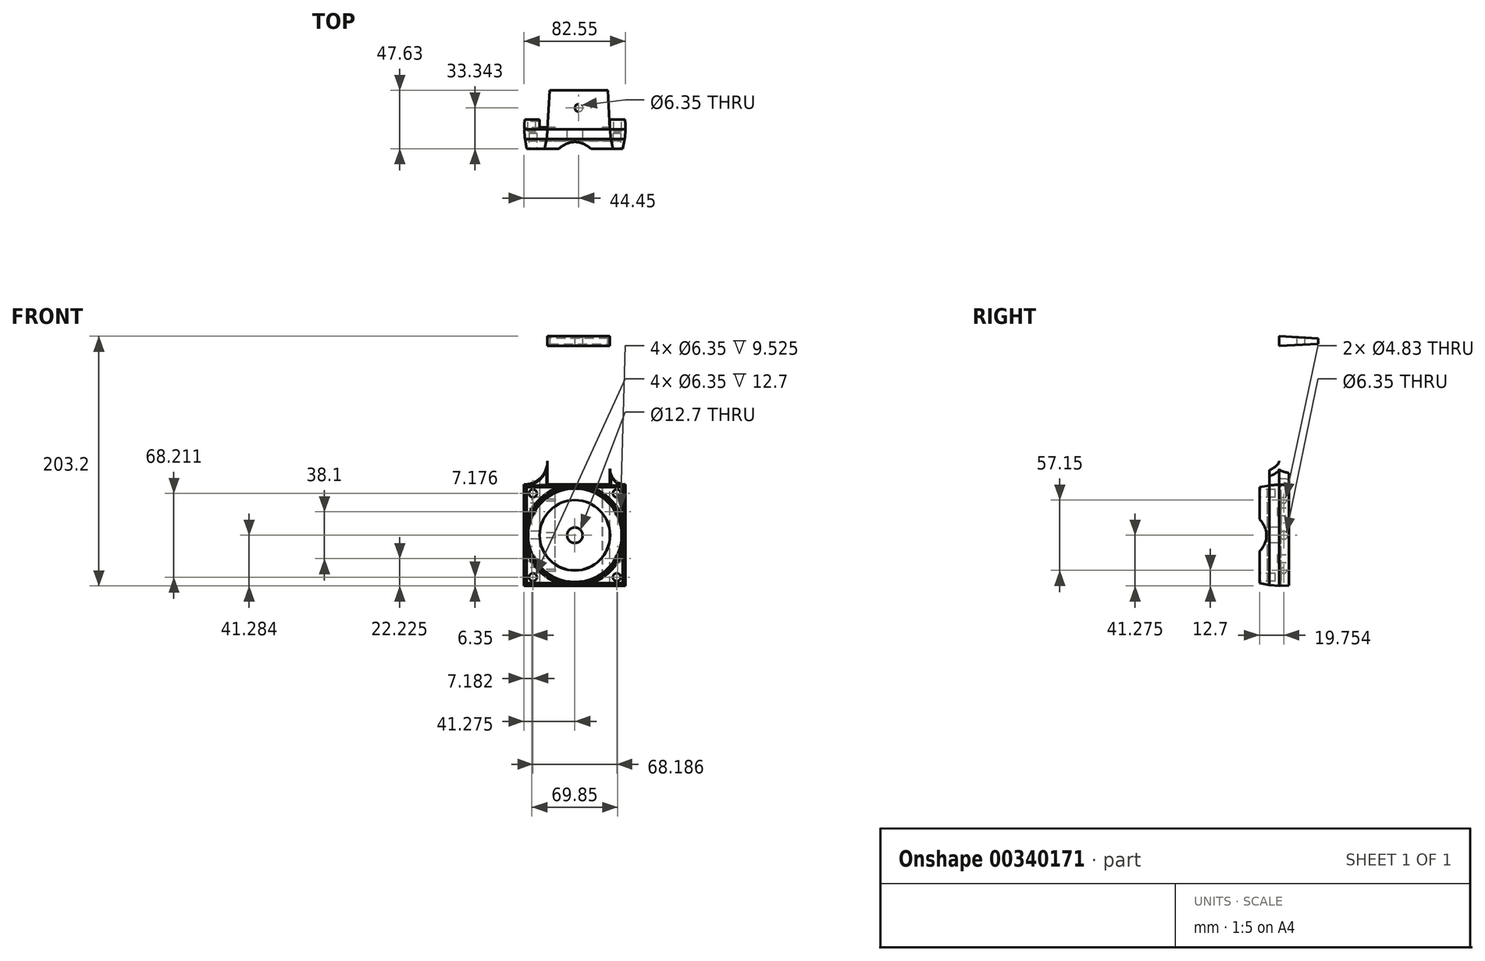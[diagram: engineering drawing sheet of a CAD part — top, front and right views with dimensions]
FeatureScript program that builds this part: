
annotation { "Feature Type Name" : "Feature", "Feature Type Description" : "" }
export const myFeature = defineFeature(function(context is Context, id is Id, definition is map)
    precondition{}
    {
        {
            var Q0;
            Q0=qCreatedBy(makeId("Front.planeOp"),FACE);
            var sketch = newSketch(context, id + "F0", { "sketchPlane" : qUnion([Q0])});
            skLineSegment(sketch, "E0.bottom", {"start": v(0, 0) * mm, "end": v(82.55, 0) * mm});
            skLineSegment(sketch, "E0.top", {"start": v(0, 82.55) * mm, "end": v(82.55, 82.55) * mm});
            skLineSegment(sketch, "E0.left", {"start": v(0, 0) * mm, "end": v(0, 82.55) * mm});
            skLineSegment(sketch, "E0.right", {"start": v(82.55, 0) * mm, "end": v(82.55, 82.55) * mm});
            skLineSegment(sketch, "E1.bottom", {"start": v(19.05, 82.55) * mm, "end": v(69.85, 82.55) * mm});
            skLineSegment(sketch, "E1.top", {"start": v(19.05, 203.2) * mm, "end": v(69.85, 203.2) * mm});
            skLineSegment(sketch, "E1.left", {"start": v(19.05, 82.55) * mm, "end": v(19.05, 203.2) * mm});
            skLineSegment(sketch, "E1.right", {"start": v(69.85, 82.55) * mm, "end": v(69.85, 203.2) * mm});
            skCircle(sketch, "E2", {"center": v(82.55, 95.25) * mm, "radius": 12.7 * mm});
            skCircle(sketch, "E3", {"center": v(0, 101.6) * mm, "radius": 19.05 * mm});
            skSolve(sketch);
        }
        {
            var Q0;
            {var subQ3=sQuery(id+"F0.wireOp",EDGE,"E1.bottom");Q0=makeQuery(id+"F0.imprint","IMPRINT",FACE,{"disambiguationData":[TD([[makeQuery(id+"F0.imprint","IMPRINT",EDGE,{"derivedFrom":subQ3}),1.0]])]});}
            var Q1;
            Q1=makeQuery(id+"F0.imprint","IMPRINT",FACE,{"disambiguationData":[TD([[makeQuery(id+"F0.imprint","IMPRINT",EDGE,{"derivedFrom":sQuery(id+"F0.wireOp",EDGE,"E0.bottom")}),1.0]])]});
            var Q2;
            {var subQ0=sQuery(id+"F0.wireOp",EDGE,"E2");var subQ3=sQuery(id+"F0.wireOp",EDGE,"E1.right");var subQ5=makeQuery(id+"F0.imprint","INTERSECT",VERTEX,{"derivedFrom":[subQ3,subQ0]});Q2=makeQuery(id+"F0.imprint","IMPRINT",FACE,{"disambiguationData":[TD([[makeQuery(id+"F0.imprint","IMPRINT",EDGE,{"disambiguationData":[TD([[subQ5,1.0]])],"derivedFrom":subQ3}),-1.0]])]});}
            var Q3;
            {var subQ0=sQuery(id+"F0.wireOp",EDGE,"E3");var subQ3=sQuery(id+"F0.wireOp",EDGE,"E1.left");var subQ5=makeQuery(id+"F0.imprint","INTERSECT",VERTEX,{"derivedFrom":[subQ3,subQ0]});Q3=makeQuery(id+"F0.imprint","IMPRINT",FACE,{"disambiguationData":[TD([[makeQuery(id+"F0.imprint","IMPRINT",EDGE,{"disambiguationData":[TD([[subQ5,1.0]])],"derivedFrom":subQ3}),1.0]])]});}
            extrude(context, id + "F1", {"entities" : qUnion([Q0, Q1, Q2, Q3]), "depth" : 7.94 * mm, "hasDraft" : true, "draftAngle" : 5 * degree, "draftPullDirection" : true});
        }
        {
            var Q0;
            Q0=makeQuery(id+"F1.opExtrude","CAP_FACE",FACE,{"disambiguationData":[OSD([sQuery(id+"F0.wireOp",EDGE,"E0.bottom"),sQuery(id+"F0.wireOp",EDGE,"E0.top"),sQuery(id+"F0.wireOp",EDGE,"E0.left"),sQuery(id+"F0.wireOp",EDGE,"E0.right"),sQuery(id+"F0.wireOp",EDGE,"E1.top"),sQuery(id+"F0.wireOp",EDGE,"E1.left"),sQuery(id+"F0.wireOp",EDGE,"E1.right")])],"isStart":true});
            var sketch = newSketch(context, id + "F2", { "sketchPlane" : qUnion([Q0])});
            skLineSegment(sketch, "E4.0", {"start": v(-19.05, 203.2) * mm, "end": v(-69.85, 203.2) * mm});
            skLineSegment(sketch, "E5", {"start": v(-69.85, 203.2) * mm, "end": v(-69.85, 195.26) * mm});
            skLineSegment(sketch, "E6", {"start": v(-69.85, 195.26) * mm, "end": v(-19.05, 195.26) * mm});
            skLineSegment(sketch, "E7", {"start": v(-19.05, 195.26) * mm, "end": v(-19.05, 203.2) * mm});
            skSolve(sketch);
        }
        {
            var Q0;
            Q0=makeQuery(id+"F2.imprint","IMPRINT",FACE,{"disambiguationData":[TD([[makeQuery(id+"F2.imprint","IMPRINT",EDGE,{"derivedFrom":sQuery(id+"F2.wireOp",EDGE,"E4.0")}),1.0]])]});
            extrude(context, id + "F3", {"entities" : qUnion([Q0]), "operationType" : NewBodyOperationType.ADD, "depth" : 31.75 * mm, "hasDraft" : true, "draftAngle" : 3 * degree, "draftPullDirection" : true});
        }
        {
            var Q0;
            Q0=makeQuery(id+"F1.opExtrude","CAP_FACE",FACE,{"disambiguationData":[OSD([sQuery(id+"F0.wireOp",EDGE,"E0.bottom"),sQuery(id+"F0.wireOp",EDGE,"E0.left"),sQuery(id+"F0.wireOp",EDGE,"E0.right"),sQuery(id+"F0.wireOp",EDGE,"E1.top"),sQuery(id+"F0.wireOp",EDGE,"E1.left"),sQuery(id+"F0.wireOp",EDGE,"E1.right"),sQuery(id+"F0.wireOp",EDGE,"E2"),sQuery(id+"F0.wireOp",EDGE,"E3")])],"isStart":true});
            var sketch = newSketch(context, id + "F4", { "sketchPlane" : qUnion([Q0])});
            skLineSegment(sketch, "E8.bottom", {"start": v(-82.55, 82.55) * mm, "end": v(-69.85, 82.55) * mm});
            skLineSegment(sketch, "E8.top", {"start": v(-82.55, 0) * mm, "end": v(-69.85, 0) * mm});
            skLineSegment(sketch, "E8.left", {"start": v(-82.55, 82.55) * mm, "end": v(-82.55, 0) * mm});
            skLineSegment(sketch, "E8.right", {"start": v(-69.85, 95.25) * mm, "end": v(-69.85, 0) * mm});
            skLineSegment(sketch, "E9.bottom", {"start": v(0, 82.55) * mm, "end": v(-12.7, 82.55) * mm});
            skLineSegment(sketch, "E9.top", {"start": v(0, 0) * mm, "end": v(-12.7, 0) * mm});
            skLineSegment(sketch, "E9.left", {"start": v(0, 82.55) * mm, "end": v(0, 0) * mm});
            skLineSegment(sketch, "E9.right", {"start": v(-12.7, 87.4) * mm, "end": v(-12.7, 0) * mm});
            skArc(sketch, "E10.0", {"start": v(-69.85, 95.25) * mm, "mid": v(-73.57, 86.27) * mm, "end": v(-82.55, 82.55) * mm});
            skArc(sketch, "E11.0", {"start": v(0, 82.55) * mm, "mid": v(-13.47, 88.13) * mm, "end": v(-19.05, 101.6) * mm});
            skSolve(sketch);
        }
        {
            var Q0;
            Q0 = qSketchRegion(id + "F4", true);
            extrude(context, id + "F5", {"entities" : qUnion([Q0]), "operationType" : NewBodyOperationType.ADD, "depth" : 7.94 * mm});
        }
        {
            var Q0;
            Q0=makeQuery(id+"F1.opExtrude","CAP_FACE",FACE,{"disambiguationData":[OSD([sQuery(id+"F0.wireOp",EDGE,"E0.bottom"),sQuery(id+"F0.wireOp",EDGE,"E0.left"),sQuery(id+"F0.wireOp",EDGE,"E0.right"),sQuery(id+"F0.wireOp",EDGE,"E1.top"),sQuery(id+"F0.wireOp",EDGE,"E1.left"),sQuery(id+"F0.wireOp",EDGE,"E1.right"),sQuery(id+"F0.wireOp",EDGE,"E2"),sQuery(id+"F0.wireOp",EDGE,"E3")])],"isStart":true});
            var sketch = newSketch(context, id + "F6", { "sketchPlane" : qUnion([Q0])});
            skLineSegment(sketch, "E12.0.0", {"start": v(-12.7, 0) * mm, "end": v(-12.7, 87.4) * mm});
            skArc(sketch, "E12.0.1", {"start": v(-12.7, 87.4) * mm, "mid": v(-17.4, 93.82) * mm, "end": v(-19.05, 101.6) * mm});
            skLineSegment(sketch, "E12.0.2", {"start": v(-19.05, 101.6) * mm, "end": v(-19.05, 195.26) * mm});
            skLineSegment(sketch, "E12.0.3", {"start": v(-69.85, 195.26) * mm, "end": v(-19.05, 195.26) * mm});
            skLineSegment(sketch, "E12.0.4", {"start": v(-69.85, 95.25) * mm, "end": v(-69.85, 195.26) * mm});
            skLineSegment(sketch, "E12.0.5", {"start": v(-69.85, 95.25) * mm, "end": v(-69.85, 0) * mm});
            skLineSegment(sketch, "E12.0.6", {"start": v(-12.7, 0) * mm, "end": v(-69.85, 0) * mm});
            skLineSegment(sketch, "E13.0.0", {"start": v(0, 0) * mm, "end": v(0, 82.55) * mm});
            skArc(sketch, "E13.0.1", {"start": v(0, 82.55) * mm, "mid": v(-6.8, 83.8) * mm, "end": v(-12.7, 87.4) * mm});
            skLineSegment(sketch, "E13.0.2", {"start": v(-12.7, 87.4) * mm, "end": v(-12.7, 0) * mm});
            skLineSegment(sketch, "E13.0.3", {"start": v(0, 0) * mm, "end": v(-12.7, 0) * mm});
            skLineSegment(sketch, "E14.0.0", {"start": v(-69.85, 0) * mm, "end": v(-69.85, 95.25) * mm});
            skArc(sketch, "E14.0.1", {"start": v(-69.85, 95.25) * mm, "mid": v(-73.57, 86.27) * mm, "end": v(-82.55, 82.55) * mm});
            skLineSegment(sketch, "E14.0.2", {"start": v(-82.55, 0) * mm, "end": v(-82.55, 82.55) * mm});
            skLineSegment(sketch, "E14.0.3", {"start": v(-69.85, 0) * mm, "end": v(-82.55, 0) * mm});
            skLineSegment(sketch, "E15.0", {"start": v(-19.05, 195.26) * mm, "end": v(-19.05, 203.2) * mm});
            skLineSegment(sketch, "E16.0", {"start": v(-19.05, 203.2) * mm, "end": v(-69.85, 203.2) * mm});
            skLineSegment(sketch, "E17.0", {"start": v(-69.85, 195.26) * mm, "end": v(-69.85, 203.2) * mm});
            skCircle(sketch, "E18", {"center": v(-82.55, 0) * mm, "radius": 254 * mm});
            skSolve(sketch);
        }
        {
            var Q0;
            Q0 = qSketchRegion(id + "F6", true);
            extrude(context, id + "F7", {"entities" : qUnion([Q0]), "operationType" : NewBodyOperationType.REMOVE, "depth" : 25.4 * mm, "hasDraft" : true, "draftAngle" : 3 * degree});
        }
        {
            var Q0;
            Q0=makeQuery(id+"F1.opExtrude","CAP_FACE",FACE,{"disambiguationData":[OSD([sQuery(id+"F0.wireOp",EDGE,"E0.bottom"),sQuery(id+"F0.wireOp",EDGE,"E0.left"),sQuery(id+"F0.wireOp",EDGE,"E0.right"),sQuery(id+"F0.wireOp",EDGE,"E1.top"),sQuery(id+"F0.wireOp",EDGE,"E1.left"),sQuery(id+"F0.wireOp",EDGE,"E1.right"),sQuery(id+"F0.wireOp",EDGE,"E2"),sQuery(id+"F0.wireOp",EDGE,"E3")])],"isStart":true});
            var sketch = newSketch(context, id + "F8", { "sketchPlane" : qUnion([Q0])});
            skLineSegment(sketch, "E19.0", {"start": v(0, 0) * mm, "end": v(0, 82.55) * mm});
            skLineSegment(sketch, "E20.0", {"start": v(-82.55, 0) * mm, "end": v(-82.55, 82.55) * mm});
            skLineSegment(sketch, "E21.0", {"start": v(-12.7, 0) * mm, "end": v(-69.85, 0) * mm});
            skLineSegment(sketch, "E22.bottom", {"start": v(0, 82.55) * mm, "end": v(-25.4, 82.55) * mm});
            skLineSegment(sketch, "E22.top", {"start": v(0, 0) * mm, "end": v(-25.4, 0) * mm});
            skLineSegment(sketch, "E22.left", {"start": v(0, 82.55) * mm, "end": v(0, 0) * mm});
            skLineSegment(sketch, "E22.right", {"start": v(-25.4, 82.55) * mm, "end": v(-25.4, 0) * mm});
            skLineSegment(sketch, "E23.bottom", {"start": v(-82.55, 82.55) * mm, "end": v(-63.5, 82.55) * mm});
            skLineSegment(sketch, "E23.top", {"start": v(-82.55, 0) * mm, "end": v(-63.5, 0) * mm});
            skLineSegment(sketch, "E23.left", {"start": v(-82.55, 82.55) * mm, "end": v(-82.55, 0) * mm});
            skLineSegment(sketch, "E23.right", {"start": v(-63.5, 82.55) * mm, "end": v(-63.5, 0) * mm});
            skSolve(sketch);
        }
        {
            var Q0;
            Q0 = qSketchRegion(id + "F8", true);
            extrude(context, id + "F9", {"entities" : qUnion([Q0]), "operationType" : NewBodyOperationType.ADD, "depth" : 1.59 * mm, "hasDraft" : true, "draftAngle" : 3 * degree, "draftPullDirection" : true});
        }
        {
            var Q0;
            Q0=makeQuery(id+"F1.opExtrude","CAP_FACE",FACE,{"disambiguationData":[OSD([sQuery(id+"F0.wireOp",EDGE,"E0.bottom"),sQuery(id+"F0.wireOp",EDGE,"E0.left"),sQuery(id+"F0.wireOp",EDGE,"E0.right"),sQuery(id+"F0.wireOp",EDGE,"E1.top"),sQuery(id+"F0.wireOp",EDGE,"E1.left"),sQuery(id+"F0.wireOp",EDGE,"E1.right"),sQuery(id+"F0.wireOp",EDGE,"E2"),sQuery(id+"F0.wireOp",EDGE,"E3")])],"isStart":false});
            var sketch = newSketch(context, id + "F10", { "sketchPlane" : qUnion([Q0])});
            skLineSegment(sketch, "E24", {"start": v(0.7, 0.7) * mm, "end": v(81.86, 81.87) * mm, "construction": true});
            skCircle(sketch, "E25", {"center": v(41.28, 41.28) * mm, "radius": 6.35 * mm});
            skSolve(sketch);
        }
        {
            var Q0;
            Q0 = qSketchRegion(id + "F10", true);
            extrude(context, id + "F11", {"entities" : qUnion([Q0]), "operationType" : NewBodyOperationType.REMOVE, "endBound" : BoundingType.THROUGH_ALL, "oppositeDirection" : true, "depth" : 25.4 * mm});
        }
        {
            var Q0;
            Q0=makeQuery(id+"F1.opExtrude","CAP_FACE",FACE,{"disambiguationData":[OSD([sQuery(id+"F0.wireOp",EDGE,"E0.bottom"),sQuery(id+"F0.wireOp",EDGE,"E0.left"),sQuery(id+"F0.wireOp",EDGE,"E0.right"),sQuery(id+"F0.wireOp",EDGE,"E1.top"),sQuery(id+"F0.wireOp",EDGE,"E1.left"),sQuery(id+"F0.wireOp",EDGE,"E1.right"),sQuery(id+"F0.wireOp",EDGE,"E2"),sQuery(id+"F0.wireOp",EDGE,"E3")])],"isStart":false});
            var sketch = newSketch(context, id + "F12", { "sketchPlane" : qUnion([Q0])});
            skCircle(sketch, "E26", {"center": v(41.28, 41.28) * mm, "radius": 28.58 * mm});
            skCircle(sketch, "E27", {"center": v(41.28, 41.28) * mm, "radius": 38.1 * mm});
            skSolve(sketch);
        }
        {
            var Q0;
            Q0 = qSketchRegion(id + "F12", true);
            extrude(context, id + "F13", {"entities" : qUnion([Q0]), "operationType" : NewBodyOperationType.ADD, "depth" : 1.59 * mm, "hasDraft" : true, "draftAngle" : 3 * degree, "draftPullDirection" : true});
        }
        {
            var Q0;
            {var subQ0=sQuery(id+"F0.wireOp",EDGE,"E0.right");var subQ1=sQuery(id+"F0.wireOp",EDGE,"E0.left");var subQ2=sQuery(id+"F0.wireOp",EDGE,"E1.top");var subQ3=sQuery(id+"F0.wireOp",EDGE,"E0.bottom");var subQ4=sQuery(id+"F0.wireOp",EDGE,"E1.left");var subQ5=sQuery(id+"F0.wireOp",EDGE,"E1.right");var subQ6=sQuery(id+"F0.wireOp",EDGE,"E2");var subQ7=sQuery(id+"F0.wireOp",EDGE,"E3");Q0=makeQuery(id+"F13.boolean.opBoolean","SPLIT",FACE,{"disambiguationData":[TD([makeQuery(id+"F1.opExtrude","SWEPT_FACE",FACE,{"disambiguationData":[OSD([subQ3])]})])],"derivedFrom":makeQuery(id+"F1.opExtrude","CAP_FACE",FACE,{"disambiguationData":[OSD([subQ3,subQ1,subQ0,subQ2,subQ4,subQ5,subQ6,subQ7])],"isStart":false})});}
            var sketch = newSketch(context, id + "F14", { "sketchPlane" : qUnion([Q0])});
            skLineSegment(sketch, "E28.0.2", {"start": v(0.7, 81.87) * mm, "end": v(0.7, 0.7) * mm});
            skLineSegment(sketch, "E28.0.3", {"start": v(0.7, 0.7) * mm, "end": v(81.86, 0.7) * mm});
            skLineSegment(sketch, "E28.0.4", {"start": v(81.86, 0.7) * mm, "end": v(81.86, 81.87) * mm});
            skLineSegment(sketch, "E29", {"start": v(0.7, 81.87) * mm, "end": v(81.86, 81.87) * mm});
            skCircle(sketch, "E30", {"center": v(41.28, 41.28) * mm, "radius": 39.69 * mm});
            skLineSegment(sketch, "E31", {"start": v(41.28, 41.28) * mm, "end": v(49.21, 41.28) * mm, "construction": true});
            skLineSegment(sketch, "E32", {"start": v(49.21, 41.28) * mm, "end": v(49.21, 42.87) * mm, "construction": true});
            skLineSegment(sketch, "E33", {"start": v(49.21, 42.87) * mm, "end": v(41.28, 41.28) * mm, "construction": true});
            skSolve(sketch);
        }
        {
            var Q0;
            Q0=makeQuery(id+"F14.imprint","IMPRINT",FACE,{"disambiguationData":[TD([[makeQuery(id+"F14.imprint","IMPRINT",EDGE,{"derivedFrom":sQuery(id+"F14.wireOp",EDGE,"E28.0.2")}),-1.0]])]});
            extrude(context, id + "F15", {"entities" : qUnion([Q0]), "operationType" : NewBodyOperationType.ADD, "depth" : 7.94 * mm, "hasDraft" : true, "draftAngle" : 11 * degree, "draftPullDirection" : true});
        }
        {
            var Q0;
            Q0=makeQuery(id+"F5.opExtrude","CAP_FACE",FACE,{"disambiguationData":[OSD([sQuery(id+"F4.wireOp",EDGE,"E8.top"),sQuery(id+"F4.wireOp",EDGE,"E8.left"),sQuery(id+"F4.wireOp",EDGE,"E8.right"),sQuery(id+"F4.wireOp",EDGE,"E10.0")])],"isStart":false});
            var sketch = newSketch(context, id + "F16", { "sketchPlane" : qUnion([Q0])});
            skCircle(sketch, "E34", {"center": v(-76.2, 22.23) * mm, "radius": 3.18 * mm});
            skCircle(sketch, "E35", {"center": v(-76.2, 60.32) * mm, "radius": 3.18 * mm});
            skCircle(sketch, "E36", {"center": v(-6.35, 60.32) * mm, "radius": 3.18 * mm});
            skCircle(sketch, "E37", {"center": v(-6.35, 22.23) * mm, "radius": 3.18 * mm});
            skSolve(sketch);
        }
        {
            var Q0;
            Q0 = qSketchRegion(id + "F16", true);
            extrude(context, id + "F17", {"entities" : qUnion([Q0]), "operationType" : NewBodyOperationType.REMOVE, "oppositeDirection" : true, "depth" : 9.52 * mm});
        }
        {
            var Q0;
            Q0=qCreatedBy(makeId("Right.planeOp"),FACE);
            var sketch = newSketch(context, id + "F18", { "sketchPlane" : qUnion([Q0])});
            skLineSegment(sketch, "E38.0", {"start": v(0, 82.55) * mm, "end": v(0, 0) * mm, "construction": true});
            skLineSegment(sketch, "E39.0", {"start": v(7.94, 86.85) * mm, "end": v(7.94, 0.42) * mm, "construction": true});
            skCircle(sketch, "E40", {"center": v(3.87, 69.85) * mm, "radius": 2.41 * mm});
            skCircle(sketch, "E41", {"center": v(3.87, 12.7) * mm, "radius": 2.41 * mm});
            skLineSegment(sketch, "E42", {"start": v(0, 41.28) * mm, "end": v(7.94, 41.28) * mm, "construction": true});
            skCircle(sketch, "E43", {"center": v(3.87, 41.28) * mm, "radius": 3.18 * mm});
            skSolve(sketch);
        }
        {
            var Q0;
            Q0 = qSketchRegion(id + "F18", true);
            extrude(context, id + "F19", {"entities" : qUnion([Q0]), "operationType" : NewBodyOperationType.REMOVE, "depth" : 25.4 * mm});
        }
        {
            var Q0;
            Q0=qCreatedBy(makeId("Top.planeOp"),FACE);
            var sketch = newSketch(context, id + "F20", { "sketchPlane" : qUnion([Q0])});
            skLineSegment(sketch, "E44.0.0", {"start": v(69.85, 0) * mm, "end": v(19.05, 0) * mm});
            skLineSegment(sketch, "E44.0.1", {"start": v(19.05, 0) * mm, "end": v(20.71, 31.75) * mm});
            skLineSegment(sketch, "E44.0.2", {"start": v(68.19, 31.75) * mm, "end": v(20.71, 31.75) * mm});
            skLineSegment(sketch, "E44.0.3", {"start": v(68.19, 31.75) * mm, "end": v(69.85, 0) * mm});
            skLineSegment(sketch, "E45", {"start": v(44.45, 31.75) * mm, "end": v(44.45, 0) * mm});
            skCircle(sketch, "E46", {"center": v(44.45, 17.46) * mm, "radius": 3.18 * mm});
            skSolve(sketch);
        }
        {
            var Q0;
            {var subQ0=sQuery(id+"F20.wireOp",EDGE,"E46");var subQ1=sQuery(id+"F20.wireOp",EDGE,"E45");var subQ2=makeQuery(id+"F20.imprint","INTERSECT",VERTEX,{"disambiguationData":[OD(0.0)],"derivedFrom":[subQ1,subQ0]});Q0=makeQuery(id+"F20.imprint","IMPRINT",FACE,{"disambiguationData":[TD([[makeQuery(id+"F20.imprint","IMPRINT",EDGE,{"disambiguationData":[TD([[subQ2,-1.0]])],"derivedFrom":subQ1}),1.0]])]});}
            var Q1;
            {var subQ0=sQuery(id+"F20.wireOp",EDGE,"E46");var subQ1=sQuery(id+"F20.wireOp",EDGE,"E45");var subQ2=makeQuery(id+"F20.imprint","INTERSECT",VERTEX,{"disambiguationData":[OD(0.0)],"derivedFrom":[subQ1,subQ0]});Q1=makeQuery(id+"F20.imprint","IMPRINT",FACE,{"disambiguationData":[TD([[makeQuery(id+"F20.imprint","IMPRINT",EDGE,{"disambiguationData":[TD([[subQ2,-1.0]])],"derivedFrom":subQ1}),-1.0]])]});}
            extrude(context, id + "F21", {"entities" : qUnion([Q0, Q1]), "operationType" : NewBodyOperationType.REMOVE, "endBound" : BoundingType.THROUGH_ALL, "depth" : 25.4 * mm});
        }
        {
            var Q0;
            Q0=makeQuery(id+"F15.*.draft.opDraft","SPLIT",FACE,{"disambiguationData":[OD(2.0)],"derivedFrom":makeQuery(id+"F15.opExtrude","CAP_FACE",FACE,{"disambiguationData":[OSD([sQuery(id+"F14.wireOp",EDGE,"E28.0.2"),sQuery(id+"F14.wireOp",EDGE,"E28.0.3"),sQuery(id+"F14.wireOp",EDGE,"E28.0.4"),sQuery(id+"F14.wireOp",EDGE,"E29"),sQuery(id+"F14.wireOp",EDGE,"E30")])],"isStart":false})});
            var sketch = newSketch(context, id + "F22", { "sketchPlane" : qUnion([Q0])});
            skLineSegment(sketch, "E47.0.0", {"start": v(2.24, 80.32) * mm, "end": v(2.24, 54.55) * mm});
            skArc(sketch, "E47.0.1", {"start": v(2.24, 54.55) * mm, "mid": v(12.13, 70.44) * mm, "end": v(28.02, 80.33) * mm});
            skLineSegment(sketch, "E47.0.2", {"start": v(28.02, 80.33) * mm, "end": v(2.24, 80.32) * mm});
            skLineSegment(sketch, "E48.0.0", {"start": v(80.31, 80.33) * mm, "end": v(54.52, 80.33) * mm});
            skArc(sketch, "E48.0.1", {"start": v(54.52, 80.33) * mm, "mid": v(70.42, 70.45) * mm, "end": v(80.31, 54.55) * mm});
            skLineSegment(sketch, "E48.0.2", {"start": v(80.31, 54.55) * mm, "end": v(80.31, 80.33) * mm});
            skLineSegment(sketch, "E49.0.0", {"start": v(80.31, 2.24) * mm, "end": v(80.31, 28.02) * mm});
            skArc(sketch, "E49.0.1", {"start": v(80.31, 28.02) * mm, "mid": v(70.42, 12.12) * mm, "end": v(54.52, 2.24) * mm});
            skLineSegment(sketch, "E49.0.2", {"start": v(54.52, 2.24) * mm, "end": v(80.31, 2.24) * mm});
            skLineSegment(sketch, "E50.0.0", {"start": v(2.24, 2.24) * mm, "end": v(28.03, 2.24) * mm});
            skArc(sketch, "E50.0.1", {"start": v(28.03, 2.24) * mm, "mid": v(12.13, 12.12) * mm, "end": v(2.24, 28.02) * mm});
            skLineSegment(sketch, "E50.0.2", {"start": v(2.24, 28.02) * mm, "end": v(2.24, 2.24) * mm});
            skLineSegment(sketch, "E51", {"start": v(2.24, 80.32) * mm, "end": v(12.13, 70.44) * mm});
            skLineSegment(sketch, "E52", {"start": v(12.13, 70.44) * mm, "end": v(70.42, 70.44) * mm});
            skLineSegment(sketch, "E53", {"start": v(70.42, 70.44) * mm, "end": v(80.31, 80.33) * mm});
            skLineSegment(sketch, "E54", {"start": v(80.31, 2.24) * mm, "end": v(70.42, 12.12) * mm});
            skLineSegment(sketch, "E55", {"start": v(70.42, 12.12) * mm, "end": v(12.13, 12.12) * mm});
            skLineSegment(sketch, "E56", {"start": v(12.13, 12.12) * mm, "end": v(2.24, 2.24) * mm});
            skCircle(sketch, "E57", {"center": v(7.18, 75.38) * mm, "radius": 3.18 * mm});
            skCircle(sketch, "E58", {"center": v(75.37, 75.39) * mm, "radius": 3.18 * mm});
            skCircle(sketch, "E59", {"center": v(75.37, 7.18) * mm, "radius": 3.18 * mm});
            skCircle(sketch, "E60", {"center": v(7.19, 7.18) * mm, "radius": 3.18 * mm});
            skSolve(sketch);
        }
        {
            var Q0;
            {var subQ0=sQuery(id+"F22.wireOp",EDGE,"E57");var subQ1=sQuery(id+"F22.wireOp",EDGE,"E51");var subQ2=makeQuery(id+"F22.imprint","INTERSECT",VERTEX,{"disambiguationData":[OD(0.0)],"derivedFrom":[subQ1,subQ0]});Q0=makeQuery(id+"F22.imprint","IMPRINT",FACE,{"disambiguationData":[TD([[makeQuery(id+"F22.imprint","IMPRINT",EDGE,{"disambiguationData":[TD([[subQ2,-1.0]])],"derivedFrom":subQ1}),1.0]])]});}
            var Q1;
            {var subQ0=sQuery(id+"F22.wireOp",EDGE,"E57");var subQ1=sQuery(id+"F22.wireOp",EDGE,"E51");var subQ2=makeQuery(id+"F22.imprint","INTERSECT",VERTEX,{"disambiguationData":[OD(0.0)],"derivedFrom":[subQ1,subQ0]});Q1=makeQuery(id+"F22.imprint","IMPRINT",FACE,{"disambiguationData":[TD([[makeQuery(id+"F22.imprint","IMPRINT",EDGE,{"disambiguationData":[TD([[subQ2,-1.0]])],"derivedFrom":subQ1}),-1.0]])]});}
            var Q2;
            {var subQ0=sQuery(id+"F22.wireOp",EDGE,"E58");var subQ1=sQuery(id+"F22.wireOp",EDGE,"E53");var subQ2=makeQuery(id+"F22.imprint","INTERSECT",VERTEX,{"disambiguationData":[OD(0.0)],"derivedFrom":[subQ1,subQ0]});Q2=makeQuery(id+"F22.imprint","IMPRINT",FACE,{"disambiguationData":[TD([[makeQuery(id+"F22.imprint","IMPRINT",EDGE,{"disambiguationData":[TD([[subQ2,-1.0]])],"derivedFrom":subQ1}),1.0]])]});}
            var Q3;
            {var subQ0=sQuery(id+"F22.wireOp",EDGE,"E58");var subQ1=sQuery(id+"F22.wireOp",EDGE,"E53");var subQ2=makeQuery(id+"F22.imprint","INTERSECT",VERTEX,{"disambiguationData":[OD(0.0)],"derivedFrom":[subQ1,subQ0]});Q3=makeQuery(id+"F22.imprint","IMPRINT",FACE,{"disambiguationData":[TD([[makeQuery(id+"F22.imprint","IMPRINT",EDGE,{"disambiguationData":[TD([[subQ2,-1.0]])],"derivedFrom":subQ1}),-1.0]])]});}
            var Q4;
            {var subQ0=sQuery(id+"F22.wireOp",EDGE,"E59");var subQ1=sQuery(id+"F22.wireOp",EDGE,"E54");var subQ2=makeQuery(id+"F22.imprint","INTERSECT",VERTEX,{"disambiguationData":[OD(0.0)],"derivedFrom":[subQ1,subQ0]});Q4=makeQuery(id+"F22.imprint","IMPRINT",FACE,{"disambiguationData":[TD([[makeQuery(id+"F22.imprint","IMPRINT",EDGE,{"disambiguationData":[TD([[subQ2,-1.0]])],"derivedFrom":subQ1}),-1.0]])]});}
            var Q5;
            {var subQ0=sQuery(id+"F22.wireOp",EDGE,"E59");var subQ1=sQuery(id+"F22.wireOp",EDGE,"E54");var subQ2=makeQuery(id+"F22.imprint","INTERSECT",VERTEX,{"disambiguationData":[OD(0.0)],"derivedFrom":[subQ1,subQ0]});Q5=makeQuery(id+"F22.imprint","IMPRINT",FACE,{"disambiguationData":[TD([[makeQuery(id+"F22.imprint","IMPRINT",EDGE,{"disambiguationData":[TD([[subQ2,-1.0]])],"derivedFrom":subQ1}),1.0]])]});}
            var Q6;
            {var subQ0=sQuery(id+"F22.wireOp",EDGE,"E60");var subQ1=sQuery(id+"F22.wireOp",EDGE,"E56");var subQ2=makeQuery(id+"F22.imprint","INTERSECT",VERTEX,{"disambiguationData":[OD(0.0)],"derivedFrom":[subQ1,subQ0]});Q6=makeQuery(id+"F22.imprint","IMPRINT",FACE,{"disambiguationData":[TD([[makeQuery(id+"F22.imprint","IMPRINT",EDGE,{"disambiguationData":[TD([[subQ2,-1.0]])],"derivedFrom":subQ1}),-1.0]])]});}
            var Q7;
            {var subQ0=sQuery(id+"F22.wireOp",EDGE,"E60");var subQ1=sQuery(id+"F22.wireOp",EDGE,"E56");var subQ2=makeQuery(id+"F22.imprint","INTERSECT",VERTEX,{"disambiguationData":[OD(0.0)],"derivedFrom":[subQ1,subQ0]});Q7=makeQuery(id+"F22.imprint","IMPRINT",FACE,{"disambiguationData":[TD([[makeQuery(id+"F22.imprint","IMPRINT",EDGE,{"disambiguationData":[TD([[subQ2,-1.0]])],"derivedFrom":subQ1}),1.0]])]});}
            extrude(context, id + "F23", {"entities" : qUnion([Q0, Q1, Q2, Q3, Q4, Q5, Q6, Q7]), "operationType" : NewBodyOperationType.REMOVE, "oppositeDirection" : true, "depth" : 12.7 * mm});
        }
    });
